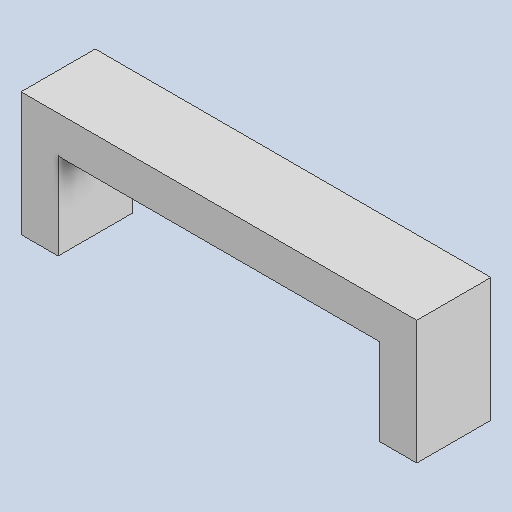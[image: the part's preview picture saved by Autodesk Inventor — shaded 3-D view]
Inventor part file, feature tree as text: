
AUTODESK INVENTOR PART (.ipt)
format: ipt  version: 2025.2 (Build 292293000, 293)  size: 92,672 bytes
history: native  units: mm
features: extrude x1, sketch x1
ambient origin geometry x8: Origin, YZ Plane, XZ Plane, XY Plane, X Axis, Y Axis, Z Axis, Center Point
bodies: Solid1 (feature_tree)
feature tree (2):
  extrude  "Extrusion1"  Depth=3.5mm
  sketch  "Sketch1"  dims[d0=1.5mm d1=3.5mm d2=13.0mm d3=1.5mm d5=3.0mm d6=0.0mm d7=1.5mm]
